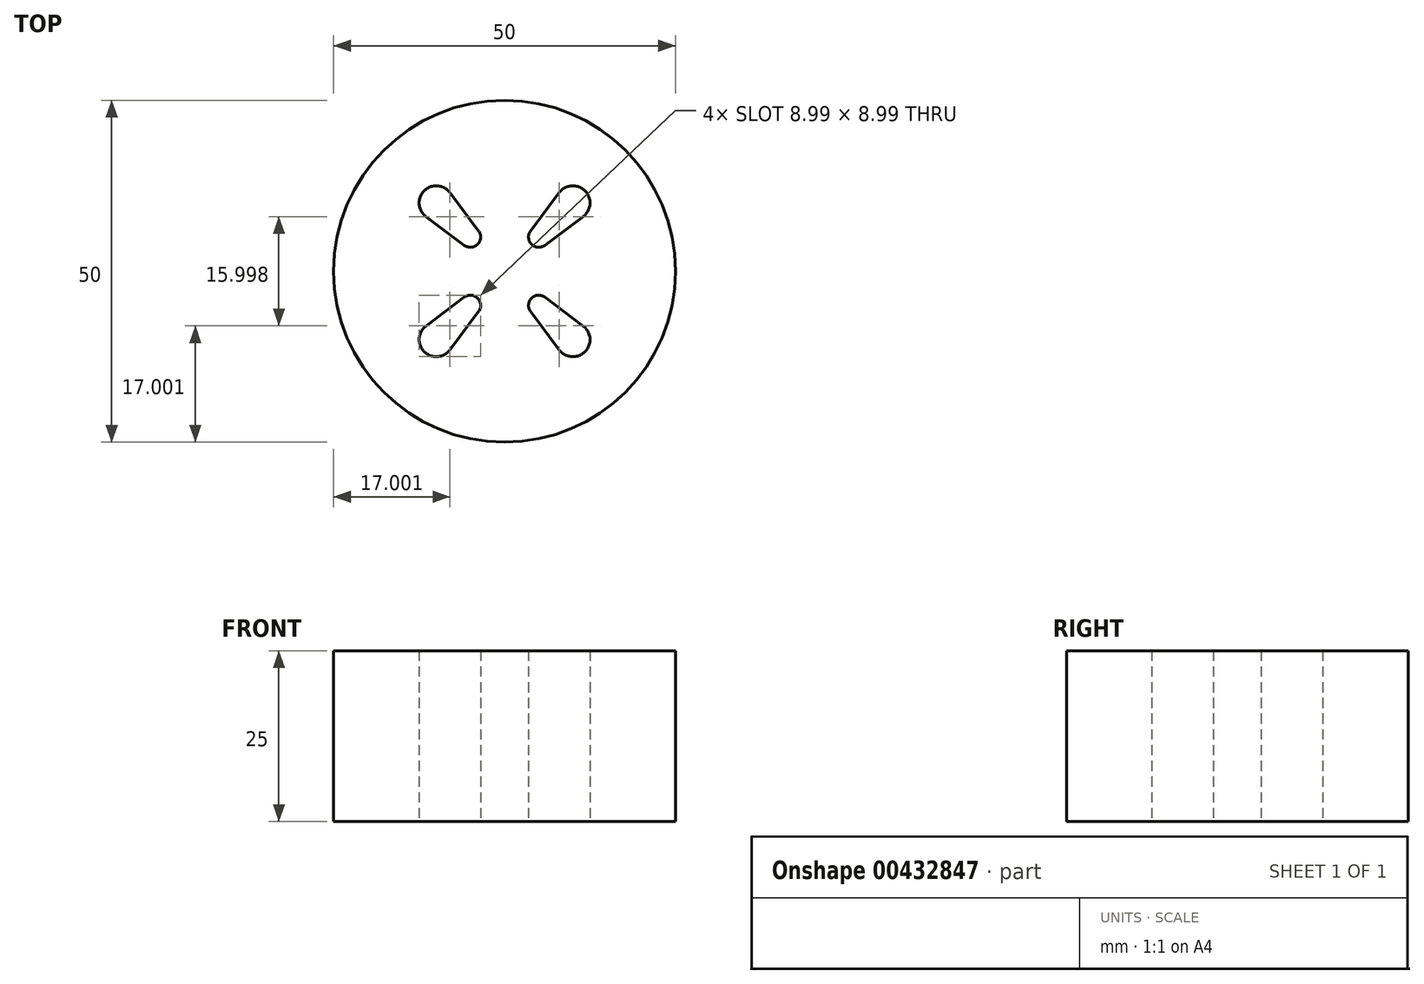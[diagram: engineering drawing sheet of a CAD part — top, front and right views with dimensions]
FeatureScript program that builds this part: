
annotation { "Feature Type Name" : "Feature", "Feature Type Description" : "" }
export const myFeature = defineFeature(function(context is Context, id is Id, definition is map)
    precondition{}
    {
        {
            var Q0;
            Q0=qCreatedBy(makeId("Top.planeOp"),FACE);
            var sketch = newSketch(context, id + "F0", { "sketchPlane" : qUnion([Q0])});
            skCircle(sketch, "E0", {"center": v(0, 0) * mm, "radius": 25 * mm});
            skArc(sketch, "E1", {"start": v(-8, 11.5) * mm, "mid": v(-11.77, 11.77) * mm, "end": v(-11.5, 8) * mm});
            skArc(sketch, "E2", {"start": v(-5.9, 3.8) * mm, "mid": v(-3.94, 3.94) * mm, "end": v(-3.8, 5.9) * mm});
            skLineSegment(sketch, "E3", {"start": v(0, 0) * mm, "end": v(0, 33.84) * mm, "construction": true});
            skLineSegment(sketch, "E4", {"start": v(0, 0) * mm, "end": v(40.18, 0) * mm, "construction": true});
            skLineSegment(sketch, "E5", {"start": v(-8, 11.5) * mm, "end": v(-3.8, 5.9) * mm});
            skLineSegment(sketch, "E6", {"start": v(-11.5, 8) * mm, "end": v(-5.9, 3.8) * mm});
            skLineSegment(sketch, "E7.MirrorCS", {"start": v(8, 11.5) * mm, "end": v(3.8, 5.9) * mm});
            skArc(sketch, "E8.MirrorCS", {"start": v(8, 11.5) * mm, "mid": v(11.77, 11.77) * mm, "end": v(11.5, 8) * mm});
            skArc(sketch, "E9.MirrorCS", {"start": v(5.9, 3.8) * mm, "mid": v(3.94, 3.94) * mm, "end": v(3.8, 5.9) * mm});
            skLineSegment(sketch, "E10.MirrorCS", {"start": v(11.5, 8) * mm, "end": v(5.9, 3.8) * mm});
            skLineSegment(sketch, "E11.MirrorCS", {"start": v(8, -11.5) * mm, "end": v(3.8, -5.9) * mm});
            skLineSegment(sketch, "E12.MirrorCS", {"start": v(11.5, -8) * mm, "end": v(5.9, -3.8) * mm});
            skArc(sketch, "E13.MirrorCS", {"start": v(5.9, -3.8) * mm, "mid": v(3.94, -3.94) * mm, "end": v(3.8, -5.9) * mm});
            skArc(sketch, "E14.MirrorCS", {"start": v(-5.9, -3.8) * mm, "mid": v(-3.94, -3.94) * mm, "end": v(-3.8, -5.9) * mm});
            skLineSegment(sketch, "E15.MirrorCS", {"start": v(-11.5, -8) * mm, "end": v(-5.9, -3.8) * mm});
            skLineSegment(sketch, "E16.MirrorCS", {"start": v(-8, -11.5) * mm, "end": v(-3.8, -5.9) * mm});
            skArc(sketch, "E17.MirrorCS", {"start": v(-8, -11.5) * mm, "mid": v(-11.77, -11.77) * mm, "end": v(-11.5, -8) * mm});
            skArc(sketch, "E18.MirrorCS", {"start": v(8, -11.5) * mm, "mid": v(11.77, -11.77) * mm, "end": v(11.5, -8) * mm});
            skSolve(sketch);
        }
        {
            var Q0;
            Q0=makeQuery(id+"F0.imprint","IMPRINT",FACE,{"disambiguationData":[TD([[makeQuery(id+"F0.imprint","IMPRINT",EDGE,{"derivedFrom":sQuery(id+"F0.wireOp",EDGE,"E0")}),1.0]])]});
            extrude(context, id + "F1", {"entities" : qUnion([Q0]), "depth" : 25 * mm});
        }
    });
